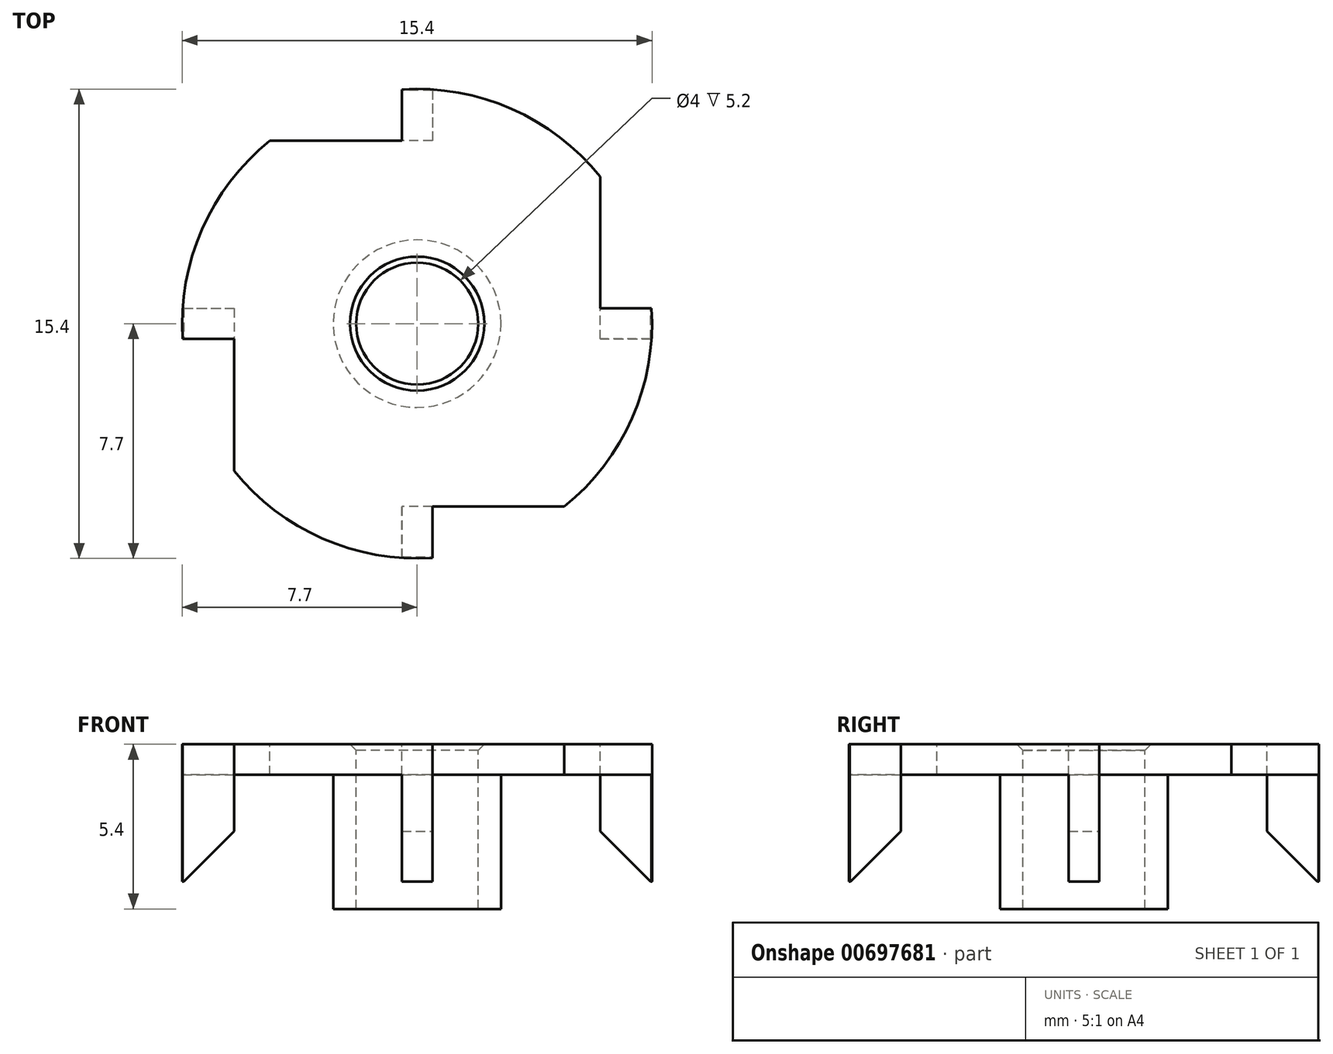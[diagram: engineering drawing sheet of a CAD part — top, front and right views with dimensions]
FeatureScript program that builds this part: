
annotation { "Feature Type Name" : "Feature", "Feature Type Description" : "" }
export const myFeature = defineFeature(function(context is Context, id is Id, definition is map)
    precondition{}
    {
        {
            var Q0;
            Q0=qCreatedBy(makeId("Top.planeOp"),FACE);
            cPlane(context, id + "F0", {"entities" : qUnion([Q0]), "cplaneType" : CPlaneType.OFFSET, "offset" : 13 * mm, "width" : 150 * mm, "height" : 150 * mm});
        }
        {
            var Q0;
            Q0=qCreatedBy(id+"F0.planeOp",FACE);
            var sketch = newSketch(context, id + "F1", { "sketchPlane" : qUnion([Q0])});
            skCircle(sketch, "E0", {"center": v(0, 0) * mm, "radius": 2.75 * mm});
            skCircle(sketch, "E1", {"center": v(0, 0) * mm, "radius": 2 * mm});
            skSolve(sketch);
        }
        {
            var Q0;
            Q0 = qSketchRegion(id + "F1", true);
            extrude(context, id + "F2", {"entities" : qUnion([Q0]), "oppositeDirection" : true, "depth" : 5.4 * mm, "offsetDistance" : 25 * mm});
        }
        {
            var Q0;
            Q0=qCreatedBy(makeId("Top.planeOp"),FACE);
            cPlane(context, id + "F3", {"entities" : qUnion([Q0]), "cplaneType" : CPlaneType.OFFSET, "offset" : 13 * mm, "width" : 150 * mm, "height" : 150 * mm});
        }
        {
            var Q0;
            Q0=qCreatedBy(id+"F3.planeOp",FACE);
            var sketch = newSketch(context, id + "F4", { "sketchPlane" : qUnion([Q0])});
            skCircle(sketch, "E2.0", {"center": v(0, 0) * mm, "radius": 2 * mm});
            skCircle(sketch, "E3", {"center": v(0, 0) * mm, "radius": 7.7 * mm});
            skSolve(sketch);
        }
        {
            var Q0;
            Q0 = qSketchRegion(id + "F4", true);
            extrude(context, id + "F5", {"entities" : qUnion([Q0]), "operationType" : NewBodyOperationType.ADD, "oppositeDirection" : true, "depth" : 1 * mm, "offsetDistance" : 25 * mm});
        }
        {
            var Q0;
            Q0=qCreatedBy(makeId("Top.planeOp"),FACE);
            cPlane(context, id + "F6", {"entities" : qUnion([Q0]), "cplaneType" : CPlaneType.OFFSET, "offset" : 13 * mm, "width" : 150 * mm, "height" : 150 * mm});
        }
        {
            var Q0;
            Q0=qCreatedBy(id+"F6.planeOp",FACE);
            var sketch = newSketch(context, id + "F7", { "sketchPlane" : qUnion([Q0])});
            skLineSegment(sketch, "E4", {"start": v(-0.5, 7.68) * mm, "end": v(-0.5, 6) * mm});
            skLineSegment(sketch, "E5", {"start": v(-0.5, 6) * mm, "end": v(-4.83, 6) * mm});
            skLineSegment(sketch, "E6", {"start": v(-7.68, -0.5) * mm, "end": v(-6, -0.5) * mm});
            skLineSegment(sketch, "E7", {"start": v(-6, -0.5) * mm, "end": v(-6, -4.83) * mm});
            skArc(sketch, "E8.trimOffspring", {"start": v(-7.68, -0.5) * mm, "mid": v(-7.18, -2.8) * mm, "end": v(-6, -4.83) * mm});
            skArc(sketch, "E9.0", {"start": v(-0.5, 7.68) * mm, "mid": v(-2.8, 7.18) * mm, "end": v(-4.83, 6) * mm});
            skLineSegment(sketch, "E10", {"start": v(0.5, -7.68) * mm, "end": v(0.5, -6) * mm});
            skLineSegment(sketch, "E11", {"start": v(0.5, -6) * mm, "end": v(4.83, -6) * mm});
            skLineSegment(sketch, "E12", {"start": v(6, 4.83) * mm, "end": v(6, 0.5) * mm});
            skLineSegment(sketch, "E13", {"start": v(6, 0.5) * mm, "end": v(7.68, 0.5) * mm});
            skArc(sketch, "E14.trimOffspring", {"start": v(7.68, 0.5) * mm, "mid": v(7.18, 2.8) * mm, "end": v(6, 4.83) * mm});
            skArc(sketch, "E15.trimOffspring", {"start": v(0.5, -7.68) * mm, "mid": v(2.8, -7.18) * mm, "end": v(4.83, -6) * mm});
            skSolve(sketch);
        }
        {
            var Q0;
            Q0 = qSketchRegion(id + "F7", true);
            extrude(context, id + "F8", {"entities" : qUnion([Q0]), "operationType" : NewBodyOperationType.REMOVE, "oppositeDirection" : true, "depth" : 213 * mm, "offsetDistance" : 25 * mm});
        }
        {
            var Q0;
            Q0=qCreatedBy(makeId("Top.planeOp"),FACE);
            cPlane(context, id + "F9", {"entities" : qUnion([Q0]), "cplaneType" : CPlaneType.OFFSET, "offset" : (13 - 1) * mm, "width" : 150 * mm, "height" : 150 * mm});
        }
        {
            var Q0;
            Q0=qCreatedBy(id+"F9.planeOp",FACE);
            var sketch = newSketch(context, id + "F10", { "sketchPlane" : qUnion([Q0])});
            skCircle(sketch, "E16.0", {"center": v(0, 0) * mm, "radius": 2 * mm, "construction": true});
            skArc(sketch, "E17", {"start": v(-7.68, 0.5) * mm, "mid": v(-7.7, 0) * mm, "end": v(-7.68, -0.5) * mm});
            skLineSegment(sketch, "E18.0", {"start": v(-7.68, -0.5) * mm, "end": v(-6, -0.5) * mm});
            skLineSegment(sketch, "E19.0", {"start": v(-0.5, 7.68) * mm, "end": v(-0.5, 6) * mm});
            skLineSegment(sketch, "E20.0", {"start": v(6, 0.5) * mm, "end": v(7.68, 0.5) * mm});
            skLineSegment(sketch, "E21.0", {"start": v(0.5, -7.68) * mm, "end": v(0.5, -6) * mm});
            skLineSegment(sketch, "E22.0", {"start": v(-0.5, -7.68) * mm, "end": v(-0.5, -6) * mm});
            skLineSegment(sketch, "E23.0", {"start": v(-7.68, 0.5) * mm, "end": v(-6, 0.5) * mm});
            skLineSegment(sketch, "E24.0", {"start": v(0.5, 7.68) * mm, "end": v(0.5, 6) * mm});
            skLineSegment(sketch, "E25.0", {"start": v(6, -0.5) * mm, "end": v(7.68, -0.5) * mm});
            skLineSegment(sketch, "E26", {"start": v(0.5, 6) * mm, "end": v(-0.5, 6) * mm});
            skLineSegment(sketch, "E27", {"start": v(-6, 0.5) * mm, "end": v(-6, -0.5) * mm});
            skLineSegment(sketch, "E28", {"start": v(0.5, -6) * mm, "end": v(-0.5, -6) * mm});
            skLineSegment(sketch, "E29", {"start": v(6, -0.5) * mm, "end": v(6, 0.5) * mm});
            skArc(sketch, "E30.trimOffspring", {"start": v(0.5, 7.68) * mm, "mid": v(0, 7.7) * mm, "end": v(-0.5, 7.68) * mm});
            skArc(sketch, "E31.trimOffspring", {"start": v(7.68, -0.5) * mm, "mid": v(7.7, 0) * mm, "end": v(7.68, 0.5) * mm});
            skArc(sketch, "E32.trimOffspring", {"start": v(-0.5, -7.68) * mm, "mid": v(0, -7.7) * mm, "end": v(0.5, -7.68) * mm});
            skSolve(sketch);
        }
        {
            var Q0;
            Q0 = qSketchRegion(id + "F10", true);
            extrude(context, id + "F11", {"entities" : qUnion([Q0]), "operationType" : NewBodyOperationType.ADD, "oppositeDirection" : true, "depth" : (4.5 - 1) * mm, "offsetDistance" : 25 * mm});
        }
        {
            var Q0;
            Q0=makeQuery(id+"F11.opExtrude","CAP_EDGE",EDGE,{"disambiguationData":[OSD([sQuery(id+"F10.wireOp",EDGE,"E27")])],"isStart":false});
            var Q1;
            Q1=makeQuery(id+"F11.opExtrude","CAP_EDGE",EDGE,{"disambiguationData":[OSD([sQuery(id+"F10.wireOp",EDGE,"E26")])],"isStart":false});
            var Q2;
            Q2=makeQuery(id+"F11.opExtrude","CAP_EDGE",EDGE,{"disambiguationData":[OSD([sQuery(id+"F10.wireOp",EDGE,"E29")])],"isStart":false});
            var Q3;
            Q3=makeQuery(id+"F11.opExtrude","CAP_EDGE",EDGE,{"disambiguationData":[OSD([sQuery(id+"F10.wireOp",EDGE,"E28")])],"isStart":false});
            chamfer(context, id + "F12", {"entities" : qUnion([Q0, Q1, Q2, Q3]), "width" : 1.65 * mm, "tangentPropagation" : true});
        }
        {
            var Q0;
            Q0=makeQuery(id+"F2.opExtrude","CAP_EDGE",EDGE,{"disambiguationData":[OSD([sQuery(id+"F1.wireOp",EDGE,"E1")])],"isStart":true});
            chamfer(context, id + "F13", {"entities" : qUnion([Q0]), "width" : 0.2 * mm, "tangentPropagation" : true});
        }
    });
